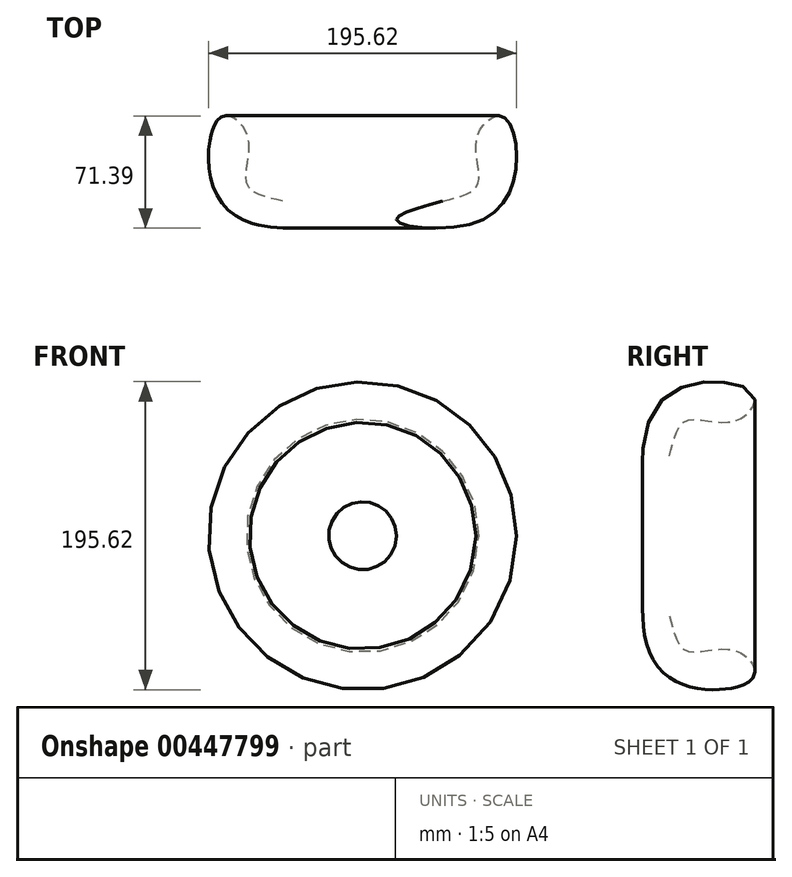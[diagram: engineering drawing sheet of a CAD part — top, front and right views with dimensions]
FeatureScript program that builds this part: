
annotation { "Feature Type Name" : "Feature", "Feature Type Description" : "" }
export const myFeature = defineFeature(function(context is Context, id is Id, definition is map)
    precondition{}
    {
        {
            var Q0;
            Q0=qCreatedBy(makeId("Top.planeOp"),FACE);
            var sketch = newSketch(context, id + "F0", { "sketchPlane" : qUnion([Q0])});
            skFitSpline(sketch, "E0", {"points": [v(20.83, -30.48) * mm, v(43.43, -19.05) * mm, v(42.67, 9.9) * mm, v(58.17, 23.62) * mm, v(67.82, -4.07) * mm, v(43.43, -43.44) * mm, v(-8.38, -42.42) * mm, v(20.83, -30.48) * mm]});
            skLineSegment(sketch, "E1", {"start": v(-29.97, -47.5) * mm, "end": v(-29.97, 37.84) * mm});
            skSolve(sketch);
        }
        {
            var Q0;
            Q0=makeQuery(id+"F0.imprint","IMPRINT",FACE,{"disambiguationData":[TD([[makeQuery(id+"F0.imprint","IMPRINT",EDGE,{"derivedFrom":sQuery(id+"F0.wireOp",EDGE,"E0")}),-1.0]])]});
            var Q1;
            Q1=sQuery(id+"F0.wireOp",EDGE,"E1");
            revolve(context, id + "F1", {"entities" : qUnion([Q0]), "axis" : qUnion([Q1]), "revolveType" : RevolveType.FULL});
        }
    });
